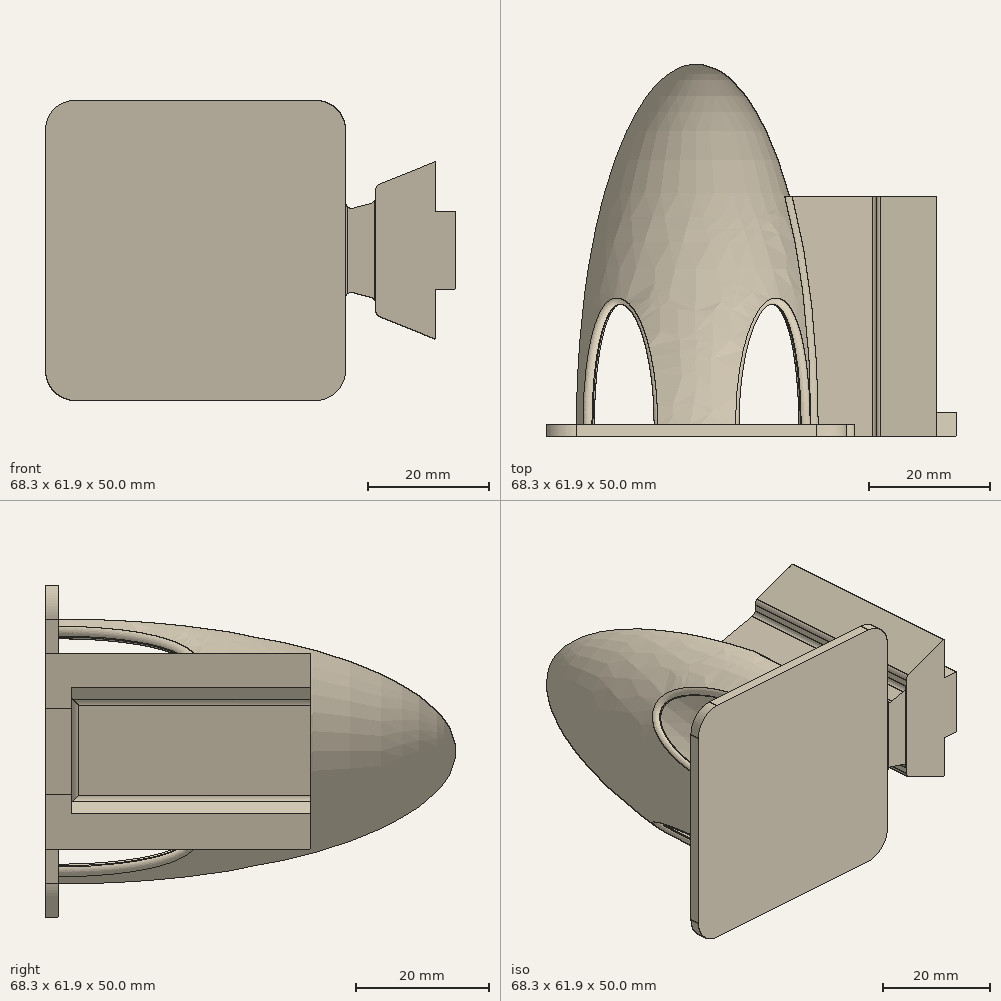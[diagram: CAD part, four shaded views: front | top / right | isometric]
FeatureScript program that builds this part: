
annotation { "Feature Type Name" : "Feature", "Feature Type Description" : "" }
export const myFeature = defineFeature(function(context is Context, id is Id, definition is map)
    precondition{}
    {
        {
            var Q0;
            Q0=qCreatedBy(makeId("Top.planeOp"),FACE);
            var sketch = newSketch(context, id + "F0", { "sketchPlane" : qUnion([Q0])});
            skEllipticalArc(sketch, "E0", {});
            skEllipticalArc(sketch, "E1", {});
            skLineSegment(sketch, "E2", {"start": v(-20, 0) * mm, "end": v(-18, 0) * mm});
            skPoint(sketch, "E2.endSnap0", {"position": v(20, 0) * mm});
            skPoint(sketch, "E3.middle", {"position": v(0, 60) * mm});
            skPoint(sketch, "E4.orphan", {"position": v(0.5, 57.5) * mm});
            skPoint(sketch, "E5.orphan", {"position": v(-0.5, 57.5) * mm});
            skPoint(sketch, "E3.top.end.orphan", {"position": v(-0.5, 62.5) * mm});
            skPoint(sketch, "E3.top.start.orphan", {"position": v(0.5, 62.5) * mm});
            skEllipticalArc(sketch, "E6.trimOffspring", {});
            skPoint(sketch, "E7.orphan", {"position": v(28.84, 0) * mm});
            skPoint(sketch, "E8.orphan", {"position": v(-25.2, 0) * mm});
            skLineSegment(sketch, "E9", {"start": v(0, -14.74) * mm, "end": v(0, 70.43) * mm, "construction": true});
            skLineSegment(sketch, "E10.left", {"start": v(1, 57.91) * mm, "end": v(1, 59.92) * mm});
            skLineSegment(sketch, "E10.right", {"start": v(-1, 57.91) * mm, "end": v(-1, 59.92) * mm});
            skPoint(sketch, "E11.orphan", {"position": v(-1, 58.5) * mm});
            skPoint(sketch, "E12.orphan", {"position": v(1, 58.5) * mm});
            skEllipticalArc(sketch, "E13.trimOffspring", {});
            skPoint(sketch, "E14.orphan", {"position": v(1, 61.5) * mm});
            skPoint(sketch, "E10.top.end.orphan", {"position": v(-1, 61.5) * mm});
            skLineSegment(sketch, "E15.trimOffspring", {"start": v(18, 0) * mm, "end": v(20, 0) * mm});
            const initialGuessF0  = {"E0": [0, 0, 0, 1, 0.06, 0.02, 0.05002085680577006, 1.5707963267948966], "E1": [0, 0, 0, -1, 0.058, 0.018, 1.5707963267948966, 3.086008480308876], "E6.trimOffspring": [0, 0, 0, 1, 0.06, 0.02, 4.71238898038469, 6.233164450373817], "E13.trimOffspring": [0, 0, 0, -1, 0.058, 0.018, 3.197176826870708, 4.71238898038469]};
            skSetInitialGuess(sketch, initialGuessF0);
            skSolve(sketch);
        }
        {
            var Q0;
            {var subQ0=sQuery(id+"F0.wireOp",EDGE,"E0");Q0=makeQuery(id+"F0.imprint","IMPRINT",FACE,{"disambiguationData":[TD([[makeQuery(id+"F0.imprint","IMPRINT",EDGE,{"derivedFrom":subQ0}),1.0]])]});}
            var Q1;
            {var subQ3=sQuery(id+"F0.wireOp",EDGE,"E3.left");Q1=makeQuery(id+"F0.imprint","IMPRINT",FACE,{"disambiguationData":[TD([[makeQuery(id+"F0.imprint","IMPRINT",EDGE,{"derivedFrom":subQ3}),-1.0]])]});}
            var Q2;
            Q2 = qSketchRegion(id + "F3", true);
            var Q3;
            Q3=sQuery(id+"F0.wireOp",EDGE,"E9");
            revolve(context, id + "F1", {"entities" : qUnion([Q0, Q1, Q2]), "axis" : qUnion([Q3]), "revolveType" : RevolveType.FULL, "surfaceOperationType" : NewSurfaceOperationType.NEW});
        }
        {
            var Q0;
            Q0=qCreatedBy(makeId("Top.planeOp"),FACE);
            var Q1;
            Q1=qCreatedBy(makeId("Right.planeOp"),FACE);
            cPlane(context, id + "F2", {"entities" : qUnion([Q0, Q1]), "cplaneType" : CPlaneType.MID_PLANE, "offset" : 25 * mm, "width" : 150 * mm, "height" : 150 * mm});
        }
        {
            var Q0;
            Q0=qCreatedBy(id+"F2.planeOp",FACE);
            var sketch = newSketch(context, id + "F3", { "sketchPlane" : qUnion([Q0])});
            skEllipse(sketch, "E16", {"center": v(0, 0) * mm, "majorRadius": 20 * mm, "minorRadius": 7.5 * mm, "majorAxis": v(-1, 0)});
            skSolve(sketch);
        }
        {
            var Q0;
            Q0 = qSketchRegion(id + "F3", true);
            extrude(context, id + "F4", {"entities" : qUnion([Q0]), "operationType" : NewBodyOperationType.REMOVE, "oppositeDirection" : true, "depth" : 101 * mm, "symmetric" : true});
        }
        {
            var Q0;
            Q0=qCreatedBy(makeId("Right.planeOp"),FACE);
            var Q1;
            Q1=qCreatedBy(makeId("Top.planeOp"),FACE);
            cPlane(context, id + "F5", {"entities" : qUnion([Q0, Q1]), "cplaneType" : CPlaneType.MID_PLANE, "offset" : 25 * mm, "flipAlignment" : true, "width" : 150 * mm, "height" : 150 * mm});
        }
        {
            var Q0;
            Q0=qCreatedBy(id+"F5.planeOp",FACE);
            var sketch = newSketch(context, id + "F6", { "sketchPlane" : qUnion([Q0])});
            skEllipse(sketch, "E17", {"center": v(0, 0) * mm, "majorRadius": 20 * mm, "minorRadius": 7.5 * mm, "majorAxis": v(-1, 0)});
            skSolve(sketch);
        }
        {
            var Q0;
            Q0=makeQuery(id+"F6.imprint","IMPRINT",FACE,{"disambiguationData":[TD([[makeQuery(id+"F6.imprint","IMPRINT",EDGE,{"derivedFrom":sQuery(id+"F6.wireOp",EDGE,"E17")}),1.0]])]});
            extrude(context, id + "F7", {"entities" : qUnion([Q0]), "operationType" : NewBodyOperationType.REMOVE, "oppositeDirection" : true, "depth" : 150 * mm, "symmetric" : true});
        }
        {
            var Q0;
            Q0=qCreatedBy(makeId("Front.planeOp"),FACE);
            cPlane(context, id + "F8", {"entities" : qUnion([Q0]), "cplaneType" : CPlaneType.OFFSET, "offset" : 0 * mm, "width" : 150 * mm, "height" : 150 * mm});
        }
        {
            var Q0;
            Q0=qCreatedBy(id+"F8.planeOp",FACE);
            var sketch = newSketch(context, id + "F9", { "sketchPlane" : qUnion([Q0])});
            skLineSegment(sketch, "E18.bottom", {"start": v(20, -25) * mm, "end": v(-20, -25) * mm});
            skLineSegment(sketch, "E18.top", {"start": v(20, 25) * mm, "end": v(-20, 25) * mm});
            skLineSegment(sketch, "E18.left", {"start": v(25, -20) * mm, "end": v(25, 20) * mm});
            skLineSegment(sketch, "E18.right", {"start": v(-25, -20) * mm, "end": v(-25, 20) * mm});
            skPoint(sketch, "E18.middle", {"position": v(0, 0) * mm});
            skPoint(sketch, "E19.visualSharp", {"position": v(-25, 25) * mm});
            skArc(sketch, "E19.filletArc", {"start": v(-20, 25) * mm, "mid": v(-23.54, 23.54) * mm, "end": v(-25, 20) * mm});
            skPoint(sketch, "E20.visualSharp", {"position": v(25, 25) * mm});
            skArc(sketch, "E20.filletArc", {"start": v(25, 20) * mm, "mid": v(23.54, 23.54) * mm, "end": v(20, 25) * mm});
            skPoint(sketch, "E21.visualSharp", {"position": v(25, -25) * mm});
            skArc(sketch, "E21.filletArc", {"start": v(20, -25) * mm, "mid": v(23.54, -23.54) * mm, "end": v(25, -20) * mm});
            skPoint(sketch, "E22.visualSharp", {"position": v(-25, -25) * mm});
            skArc(sketch, "E22.filletArc", {"start": v(-25, -20) * mm, "mid": v(-23.54, -23.54) * mm, "end": v(-20, -25) * mm});
            skSolve(sketch);
        }
        {
            var Q0;
            Q0 = qSketchRegion(id + "F9", true);
            extrude(context, id + "F10", {"entities" : qUnion([Q0]), "operationType" : NewBodyOperationType.ADD, "depth" : 2 * mm});
        }
        {
            var Q0;
            Q0=sQuery(id+"F9.wireOp",VERTEX,"E18.middle");
            var Q1;
            Q1=makeQuery(id+"F1.opRevolve","SWEPT_BODY",BODY,{"disambiguationData":[OSD([sQuery(id+"F0.wireOp",EDGE,"E0"),sQuery(id+"F0.wireOp",EDGE,"E2"),sQuery(id+"F0.wireOp",EDGE,"E10.right"),sQuery(id+"F0.wireOp",EDGE,"E13.trimOffspring")])]});
            hole(context, id + "F11", {"style" : HoleStyle.SIMPLE, "endStyle" : HoleEndStyle.BLIND, "oppositeDirection" : true, "holeDiameter" : 2 * mm, "holeDepth" : 1 * mm, "startFromSketch" : true, "locations" : qUnion([Q0]), "scope" : qUnion([Q1])});
        }
        {
            var Q0;
            Q0=makeQuery(id+"F10.opExtrude","CAP_FACE",FACE,{"disambiguationData":[OSD([sQuery(id+"F9.wireOp",EDGE,"E18.bottom"),sQuery(id+"F9.wireOp",EDGE,"E18.top"),sQuery(id+"F9.wireOp",EDGE,"E18.left"),sQuery(id+"F9.wireOp",EDGE,"E18.right"),sQuery(id+"F9.wireOp",EDGE,"E19.filletArc"),sQuery(id+"F9.wireOp",EDGE,"E20.filletArc"),sQuery(id+"F9.wireOp",EDGE,"E21.filletArc"),sQuery(id+"F9.wireOp",EDGE,"E22.filletArc")])],"isStart":false});
            var sketch = newSketch(context, id + "F12", { "sketchPlane" : qUnion([Q0])});
            skLineSegment(sketch, "E23", {"start": v(30, 10.75) * mm, "end": v(30, 3.84) * mm});
            skLineSegment(sketch, "E24", {"start": v(40, 14.8) * mm, "end": v(40, 6.5) * mm});
            skPoint(sketch, "E25.middle", {"position": v(30, 0) * mm});
            skLineSegment(sketch, "E26", {"start": v(30, 10.75) * mm, "end": v(40, 14.8) * mm});
            skLineSegment(sketch, "E27", {"start": v(30, -10.75) * mm, "end": v(40, -14.8) * mm});
            skLineSegment(sketch, "E28.trimOffspring", {"start": v(30, -3.84) * mm, "end": v(30, -10.75) * mm});
            skLineSegment(sketch, "E29.bottom", {"start": v(43.3, -6.5) * mm, "end": v(40, -6.5) * mm});
            skLineSegment(sketch, "E29.top", {"start": v(43.3, 6.5) * mm, "end": v(40, 6.5) * mm});
            skLineSegment(sketch, "E29.left", {"start": v(43.3, -6.5) * mm, "end": v(43.3, 6.5) * mm});
            skLineSegment(sketch, "E30.trimOffspring", {"start": v(40, -6.5) * mm, "end": v(40, -14.8) * mm});
            skLineSegment(sketch, "E31", {"start": v(30, 3.84) * mm, "end": v(30, -3.84) * mm});
            skSolve(sketch);
        }
        {
            var Q0;
            Q0 = qSketchRegion(id + "F12", true);
            extrude(context, id + "F13", {"entities" : qUnion([Q0]), "oppositeDirection" : true, "depth" : 40 * mm});
        }
        {
            var Q0;
            {var subQ0=sQuery(id+"F12.wireOp",EDGE,"E29.top");var subQ1=sQuery(id+"F12.wireOp",EDGE,"E27");var subQ2=sQuery(id+"F12.wireOp",EDGE,"E26");var subQ3=sQuery(id+"F12.wireOp",EDGE,"E29.bottom");var subQ4=sQuery(id+"F12.wireOp",EDGE,"E25.top");var subQ5=sQuery(id+"F12.wireOp",EDGE,"E25.bottom");var subQ6=sQuery(id+"F12.wireOp",EDGE,"E28.trimOffspring");var subQ7=sQuery(id+"F12.wireOp",EDGE,"E23");var subQ8=sQuery(id+"F12.wireOp",EDGE,"E24");var subQ9=sQuery(id+"F12.wireOp",EDGE,"E29.left");var subQ10=sQuery(id+"F12.wireOp",EDGE,"E30.trimOffspring");Q0=makeQuery(id+"F13.boolean.opBoolean","SPLIT",FACE,{"disambiguationData":[TD([makeQuery(id+"F1.opRevolve","SWEPT_FACE",FACE,{"disambiguationData":[OSD([sQuery(id+"F0.wireOp",EDGE,"64f7480b-f7c1-41a7-9161-91fdca635b13.0")])]})])],"derivedFrom":makeQuery(id+"F13.opExtrude","CAP_FACE",FACE,{"disambiguationData":[OSD([subQ7,subQ8,subQ5,subQ4,sQuery(id+"F12.wireOp",EDGE,"E25.left"),subQ2,subQ1,subQ6,subQ3,subQ0,subQ9,subQ10])],"isStart":false})});}
            cPlane(context, id + "F14", {"entities" : qUnion([Q0]), "cplaneType" : CPlaneType.OFFSET, "offset" : 36 * mm, "oppositeDirection" : true, "width" : 150 * mm, "height" : 150 * mm});
        }
        {
            var Q0;
            Q0=qCreatedBy(id+"F14.planeOp",FACE);
            var sketch = newSketch(context, id + "F15", { "sketchPlane" : qUnion([Q0])});
            skPoint(sketch, "E32.middle", {"position": v(-35, 0.14) * mm});
            skLineSegment(sketch, "E33", {"start": v(-35, -7.36) * mm, "end": v(-41.98, -10.18) * mm});
            skLineSegment(sketch, "E34", {"start": v(-35, 7.64) * mm, "end": v(-41.98, 10.47) * mm});
            skLineSegment(sketch, "E35", {"start": v(-35, 7.64) * mm, "end": v(-35, -7.36) * mm});
            skLineSegment(sketch, "E36", {"start": v(-41.98, -10.18) * mm, "end": v(-56.76, -10.18) * mm});
            skLineSegment(sketch, "E37", {"start": v(-56.76, -10.18) * mm, "end": v(-56.76, 10.47) * mm});
            skLineSegment(sketch, "E38", {"start": v(-56.76, 10.47) * mm, "end": v(-41.98, 10.47) * mm});
            skSolve(sketch);
        }
        {
            var Q0;
            Q0 = qSketchRegion(id + "F15", true);
            extrude(context, id + "F16", {"entities" : qUnion([Q0]), "operationType" : NewBodyOperationType.REMOVE, "depth" : 50 * mm});
        }
        {
            var Q0;
            Q0=qCreatedBy(makeId("Top.planeOp"),FACE);
            var sketch = newSketch(context, id + "F17", { "sketchPlane" : qUnion([Q0])});
            skLineSegment(sketch, "E39", {"start": v(19.26, -1.97) * mm, "end": v(32.88, -1.97) * mm});
            skLineSegment(sketch, "E40", {"start": v(32.88, -1.97) * mm, "end": v(32.88, 38) * mm});
            skLineSegment(sketch, "E41", {"start": v(32.88, 38) * mm, "end": v(14.68, 38) * mm});
            skFitSpline(sketch, "E42", {"points": [v(19.26, -1.97) * mm, v(14.68, 38) * mm], "startDerivative": vector(1.24, 41.82) * mm, "endDerivative": vector(-10.35, 36.32) * mm});
            skSolve(sketch);
        }
        {
            var Q0;
            Q0 = qSketchRegion(id + "F17", true);
            var Q1;
            Q1=sQuery(id+"F0.wireOp",EDGE,"E9");
            revolve(context, id + "F18", {"operationType" : NewBodyOperationType.ADD, "entities" : qUnion([Q0]), "axis" : qUnion([Q1]), "revolveType" : RevolveType.SYMMETRIC, "angle" : 30 * degree});
        }
        {
            var Q0;
            Q0=makeQuery(id+"F18.boolean.opBoolean","INTERSECT",EDGE,{"disambiguationData":[OD(1.0)],"derivedFrom":[makeQuery(id+"F1.opRevolve","SWEPT_FACE",FACE,{"disambiguationData":[OSD([sQuery(id+"F0.wireOp",EDGE,"E0")])]}),makeQuery(id+"F18.opRevolve","CAP_FACE",FACE,{"disambiguationData":[OSD([sQuery(id+"F17.wireOp",EDGE,"E39"),sQuery(id+"F17.wireOp",EDGE,"E40"),sQuery(id+"F17.wireOp",EDGE,"E41"),sQuery(id+"F17.wireOp",EDGE,"E42")])],"isStart":true})]});
            var Q1;
            Q1=makeQuery(id+"F18.boolean.opBoolean","INTERSECT",EDGE,{"disambiguationData":[OD(1.0)],"derivedFrom":[makeQuery(id+"F1.opRevolve","SWEPT_FACE",FACE,{"disambiguationData":[OSD([sQuery(id+"F0.wireOp",EDGE,"E0")])]}),makeQuery(id+"F18.opRevolve","CAP_FACE",FACE,{"disambiguationData":[OSD([sQuery(id+"F17.wireOp",EDGE,"E39"),sQuery(id+"F17.wireOp",EDGE,"E40"),sQuery(id+"F17.wireOp",EDGE,"E41"),sQuery(id+"F17.wireOp",EDGE,"E42")])],"isStart":false})]});
            var Q2;
            Q2=makeQuery(id+"F18.boolean.opBoolean","INTERSECT",EDGE,{"derivedFrom":[makeQuery(id+"F13.opExtrude","SWEPT_FACE",FACE,{"disambiguationData":[OSD([sQuery(id+"F12.wireOp",EDGE,"E23"),sQuery(id+"F12.wireOp",EDGE,"E28.trimOffspring"),sQuery(id+"F12.wireOp",EDGE,"E31")])]}),makeQuery(id+"F18.opRevolve","CAP_FACE",FACE,{"disambiguationData":[OSD([sQuery(id+"F17.wireOp",EDGE,"E39"),sQuery(id+"F17.wireOp",EDGE,"E40"),sQuery(id+"F17.wireOp",EDGE,"E41"),sQuery(id+"F17.wireOp",EDGE,"E42")])],"isStart":true})]});
            var Q3;
            Q3=makeQuery(id+"F18.boolean.opBoolean","INTERSECT",EDGE,{"derivedFrom":[makeQuery(id+"F13.opExtrude","SWEPT_FACE",FACE,{"disambiguationData":[OSD([sQuery(id+"F12.wireOp",EDGE,"E23"),sQuery(id+"F12.wireOp",EDGE,"E28.trimOffspring"),sQuery(id+"F12.wireOp",EDGE,"E31")])]}),makeQuery(id+"F18.opRevolve","CAP_FACE",FACE,{"disambiguationData":[OSD([sQuery(id+"F17.wireOp",EDGE,"E39"),sQuery(id+"F17.wireOp",EDGE,"E40"),sQuery(id+"F17.wireOp",EDGE,"E41"),sQuery(id+"F17.wireOp",EDGE,"E42")])],"isStart":false})]});
            var Q4;
            {var subQ0=sQuery(id+"F0.wireOp",EDGE,"E2");var subQ1=sQuery(id+"F0.wireOp",EDGE,"E1");var subQ2=makeQuery(id+"F0.imprint","INTERSECT",VERTEX,{"disambiguationData":[OD(0.0)],"derivedFrom":[subQ1,subQ0]});var subQ3=sQuery(id+"F0.wireOp",EDGE,"E6.trimOffspring");var subQ4=makeQuery(id+"F1.opRevolve","SWEPT_FACE",FACE,{"disambiguationData":[OSD([subQ0]),TDD([makeQuery(id+"F0.imprint","IMPRINT",EDGE,{"disambiguationData":[TD([[subQ2,-1.0]])],"derivedFrom":subQ0})])]});var subQ5=makeQuery(id+"F1.opRevolve","SWEPT_FACE",FACE,{"disambiguationData":[OSD([subQ3])]});var subQ6=makeQuery(id+"F4.opExtrude","SWEPT_FACE",FACE,{"disambiguationData":[OSD([sQuery(id+"F3.wireOp",EDGE,"E16")])]});var subQ8=sQuery(id+"F0.wireOp",EDGE,"E0");var subQ9=makeQuery(id+"F1.opRevolve","SWEPT_FACE",FACE,{"disambiguationData":[OSD([subQ8])]});var subQ10=makeQuery(id+"F0.imprint","INTERSECT",VERTEX,{"disambiguationData":[OD(1.0)],"derivedFrom":[subQ1,subQ0]});var subQ11=makeQuery(id+"F1.opRevolve","SWEPT_FACE",FACE,{"disambiguationData":[OSD([subQ0]),TDD([makeQuery(id+"F0.imprint","IMPRINT",EDGE,{"disambiguationData":[TD([[makeQuery(id+"F0.imprint","INTERSECT",VERTEX,{"derivedFrom":[subQ8,subQ0]}),-1.0]])],"derivedFrom":subQ0})])]});Q4=makeQuery(id+"F10.boolean.opBoolean","MERGE",EDGE,{"derivedFrom":[makeQuery(id+"F7.boolean.opBoolean","SPLIT",EDGE,{"disambiguationData":[TD([makeQuery(id+"F4.boolean.opBoolean","COPY",FACE,{"disambiguationData":[TD([subQ9,makeQuery(id+"F1.opRevolve","SWEPT_FACE",FACE,{"disambiguationData":[OSD([subQ1]),TDD([makeQuery(id+"F0.imprint","IMPRINT",EDGE,{"disambiguationData":[TD([[subQ10,1.0]])],"derivedFrom":subQ1})])]}),subQ11]),OD(0.0)],"derivedFrom":subQ6})])],"derivedFrom":makeQuery(id+"F4.boolean.opBoolean","SPLIT",EDGE,{"disambiguationData":[OD(0.0)],"derivedFrom":makeQuery(id+"F1.opRevolve","SWEPT_EDGE",EDGE,{"disambiguationData":[OSD([subQ8,subQ0])]})})}),makeQuery(id+"F7.boolean.opBoolean","SPLIT",EDGE,{"disambiguationData":[TD([makeQuery(id+"F4.boolean.opBoolean","COPY",FACE,{"disambiguationData":[TD([makeQuery(id+"F1.opRevolve","SWEPT_FACE",FACE,{"disambiguationData":[OSD([subQ1]),TDD([makeQuery(id+"F0.imprint","IMPRINT",EDGE,{"disambiguationData":[TD([[subQ2,-1.0]])],"derivedFrom":subQ1})])]}),subQ4,subQ5]),OD(0.0)],"derivedFrom":subQ6})])],"derivedFrom":makeQuery(id+"F4.boolean.opBoolean","SPLIT",EDGE,{"disambiguationData":[OD(0.0)],"derivedFrom":makeQuery(id+"F1.opRevolve","SWEPT_EDGE",EDGE,{"disambiguationData":[OSD([subQ0,subQ3])]})})})]});}
            var Q5;
            {var subQ0=sQuery(id+"F0.wireOp",EDGE,"E2");var subQ1=sQuery(id+"F0.wireOp",EDGE,"E1");var subQ2=makeQuery(id+"F0.imprint","INTERSECT",VERTEX,{"disambiguationData":[OD(0.0)],"derivedFrom":[subQ1,subQ0]});var subQ3=sQuery(id+"F0.wireOp",EDGE,"E6.trimOffspring");var subQ4=makeQuery(id+"F1.opRevolve","SWEPT_FACE",FACE,{"disambiguationData":[OSD([subQ0]),TDD([makeQuery(id+"F0.imprint","IMPRINT",EDGE,{"disambiguationData":[TD([[subQ2,-1.0]])],"derivedFrom":subQ0})])]});var subQ5=makeQuery(id+"F1.opRevolve","SWEPT_FACE",FACE,{"disambiguationData":[OSD([subQ3])]});var subQ6=makeQuery(id+"F4.opExtrude","SWEPT_FACE",FACE,{"disambiguationData":[OSD([sQuery(id+"F3.wireOp",EDGE,"E16")])]});var subQ8=sQuery(id+"F0.wireOp",EDGE,"E0");var subQ9=makeQuery(id+"F1.opRevolve","SWEPT_FACE",FACE,{"disambiguationData":[OSD([subQ8])]});var subQ10=makeQuery(id+"F0.imprint","INTERSECT",VERTEX,{"disambiguationData":[OD(1.0)],"derivedFrom":[subQ1,subQ0]});var subQ11=makeQuery(id+"F1.opRevolve","SWEPT_FACE",FACE,{"disambiguationData":[OSD([subQ0]),TDD([makeQuery(id+"F0.imprint","IMPRINT",EDGE,{"disambiguationData":[TD([[makeQuery(id+"F0.imprint","INTERSECT",VERTEX,{"derivedFrom":[subQ8,subQ0]}),-1.0]])],"derivedFrom":subQ0})])]});Q5=makeQuery(id+"F10.boolean.opBoolean","MERGE",EDGE,{"derivedFrom":[makeQuery(id+"F7.boolean.opBoolean","SPLIT",EDGE,{"disambiguationData":[TD([makeQuery(id+"F4.boolean.opBoolean","COPY",FACE,{"disambiguationData":[TD([subQ9,makeQuery(id+"F1.opRevolve","SWEPT_FACE",FACE,{"disambiguationData":[OSD([subQ1]),TDD([makeQuery(id+"F0.imprint","IMPRINT",EDGE,{"disambiguationData":[TD([[subQ10,1.0]])],"derivedFrom":subQ1})])]}),subQ11]),OD(0.0)],"derivedFrom":subQ6})])],"derivedFrom":makeQuery(id+"F4.boolean.opBoolean","SPLIT",EDGE,{"disambiguationData":[OD(1.0)],"derivedFrom":makeQuery(id+"F1.opRevolve","SWEPT_EDGE",EDGE,{"disambiguationData":[OSD([subQ8,subQ0])]})})}),makeQuery(id+"F7.boolean.opBoolean","SPLIT",EDGE,{"disambiguationData":[TD([makeQuery(id+"F4.boolean.opBoolean","COPY",FACE,{"disambiguationData":[TD([makeQuery(id+"F1.opRevolve","SWEPT_FACE",FACE,{"disambiguationData":[OSD([subQ1]),TDD([makeQuery(id+"F0.imprint","IMPRINT",EDGE,{"disambiguationData":[TD([[subQ2,-1.0]])],"derivedFrom":subQ1})])]}),subQ4,subQ5]),OD(0.0)],"derivedFrom":subQ6})])],"derivedFrom":makeQuery(id+"F4.boolean.opBoolean","SPLIT",EDGE,{"disambiguationData":[OD(1.0)],"derivedFrom":makeQuery(id+"F1.opRevolve","SWEPT_EDGE",EDGE,{"disambiguationData":[OSD([subQ0,subQ3])]})})})]});}
            var Q6;
            {var subQ0=sQuery(id+"F0.wireOp",EDGE,"E2");var subQ1=sQuery(id+"F0.wireOp",EDGE,"E1");var subQ2=makeQuery(id+"F0.imprint","INTERSECT",VERTEX,{"disambiguationData":[OD(0.0)],"derivedFrom":[subQ1,subQ0]});var subQ3=sQuery(id+"F0.wireOp",EDGE,"E6.trimOffspring");var subQ4=makeQuery(id+"F1.opRevolve","SWEPT_FACE",FACE,{"disambiguationData":[OSD([subQ0]),TDD([makeQuery(id+"F0.imprint","IMPRINT",EDGE,{"disambiguationData":[TD([[subQ2,-1.0]])],"derivedFrom":subQ0})])]});var subQ5=makeQuery(id+"F1.opRevolve","SWEPT_FACE",FACE,{"disambiguationData":[OSD([subQ3])]});var subQ6=makeQuery(id+"F4.opExtrude","SWEPT_FACE",FACE,{"disambiguationData":[OSD([sQuery(id+"F3.wireOp",EDGE,"E16")])]});var subQ8=sQuery(id+"F0.wireOp",EDGE,"E0");var subQ9=makeQuery(id+"F1.opRevolve","SWEPT_FACE",FACE,{"disambiguationData":[OSD([subQ8])]});var subQ10=makeQuery(id+"F0.imprint","INTERSECT",VERTEX,{"disambiguationData":[OD(1.0)],"derivedFrom":[subQ1,subQ0]});var subQ11=makeQuery(id+"F1.opRevolve","SWEPT_FACE",FACE,{"disambiguationData":[OSD([subQ0]),TDD([makeQuery(id+"F0.imprint","IMPRINT",EDGE,{"disambiguationData":[TD([[makeQuery(id+"F0.imprint","INTERSECT",VERTEX,{"derivedFrom":[subQ8,subQ0]}),-1.0]])],"derivedFrom":subQ0})])]});Q6=makeQuery(id+"F10.boolean.opBoolean","MERGE",EDGE,{"derivedFrom":[makeQuery(id+"F7.boolean.opBoolean","SPLIT",EDGE,{"disambiguationData":[TD([makeQuery(id+"F4.boolean.opBoolean","COPY",FACE,{"disambiguationData":[TD([subQ9,makeQuery(id+"F1.opRevolve","SWEPT_FACE",FACE,{"disambiguationData":[OSD([subQ1]),TDD([makeQuery(id+"F0.imprint","IMPRINT",EDGE,{"disambiguationData":[TD([[subQ10,1.0]])],"derivedFrom":subQ1})])]}),subQ11]),OD(1.0)],"derivedFrom":subQ6})])],"derivedFrom":makeQuery(id+"F4.boolean.opBoolean","SPLIT",EDGE,{"disambiguationData":[OD(0.0)],"derivedFrom":makeQuery(id+"F1.opRevolve","SWEPT_EDGE",EDGE,{"disambiguationData":[OSD([subQ8,subQ0])]})})}),makeQuery(id+"F7.boolean.opBoolean","SPLIT",EDGE,{"disambiguationData":[TD([makeQuery(id+"F4.boolean.opBoolean","COPY",FACE,{"disambiguationData":[TD([makeQuery(id+"F1.opRevolve","SWEPT_FACE",FACE,{"disambiguationData":[OSD([subQ1]),TDD([makeQuery(id+"F0.imprint","IMPRINT",EDGE,{"disambiguationData":[TD([[subQ2,-1.0]])],"derivedFrom":subQ1})])]}),subQ4,subQ5]),OD(1.0)],"derivedFrom":subQ6})])],"derivedFrom":makeQuery(id+"F4.boolean.opBoolean","SPLIT",EDGE,{"disambiguationData":[OD(0.0)],"derivedFrom":makeQuery(id+"F1.opRevolve","SWEPT_EDGE",EDGE,{"disambiguationData":[OSD([subQ0,subQ3])]})})})]});}
            var Q7;
            Q7=makeQuery(id+"F13.opExtrude","SWEPT_EDGE",EDGE,{"disambiguationData":[OSD([sQuery(id+"F12.wireOp",EDGE,"E27"),sQuery(id+"F12.wireOp",EDGE,"E28.trimOffspring")])]});
            var Q8;
            Q8=makeQuery(id+"F13.opExtrude","SWEPT_EDGE",EDGE,{"disambiguationData":[OSD([sQuery(id+"F12.wireOp",EDGE,"E23"),sQuery(id+"F12.wireOp",EDGE,"E26")])]});
            var Q9;
            Q9=makeQuery(id+"F16.boolean.opBoolean","COPY",EDGE,{"derivedFrom":makeQuery(id+"F16.opExtrude","SWEPT_EDGE",EDGE,{"disambiguationData":[OSD([sQuery(id+"F15.wireOp",EDGE,"E33"),sQuery(id+"F15.wireOp",EDGE,"E35")])]})});
            var Q10;
            Q10=makeQuery(id+"F16.boolean.opBoolean","COPY",EDGE,{"derivedFrom":makeQuery(id+"F16.opExtrude","SWEPT_EDGE",EDGE,{"disambiguationData":[OSD([sQuery(id+"F15.wireOp",EDGE,"E34"),sQuery(id+"F15.wireOp",EDGE,"E35")])]})});
            var Q11;
            Q11=makeQuery(id+"F18.boolean.opBoolean","INTERSECT",EDGE,{"derivedFrom":[makeQuery(id+"F10.opExtrude","SWEPT_FACE",FACE,{"disambiguationData":[OSD([sQuery(id+"F9.wireOp",EDGE,"E18.left")])]}),makeQuery(id+"F18.opRevolve","CAP_FACE",FACE,{"disambiguationData":[OSD([sQuery(id+"F17.wireOp",EDGE,"E39"),sQuery(id+"F17.wireOp",EDGE,"E40"),sQuery(id+"F17.wireOp",EDGE,"E41"),sQuery(id+"F17.wireOp",EDGE,"E42")])],"isStart":true})]});
            var Q12;
            Q12=makeQuery(id+"F18.boolean.opBoolean","INTERSECT",EDGE,{"derivedFrom":[makeQuery(id+"F10.opExtrude","SWEPT_FACE",FACE,{"disambiguationData":[OSD([sQuery(id+"F9.wireOp",EDGE,"E18.left")])]}),makeQuery(id+"F18.opRevolve","SWEPT_FACE",FACE,{"disambiguationData":[OSD([sQuery(id+"F17.wireOp",EDGE,"E39")])]})]});
            var Q13;
            Q13=makeQuery(id+"F18.boolean.opBoolean","INTERSECT",EDGE,{"derivedFrom":[makeQuery(id+"F13.opExtrude","SWEPT_FACE",FACE,{"disambiguationData":[OSD([sQuery(id+"F12.wireOp",EDGE,"E23"),sQuery(id+"F12.wireOp",EDGE,"E28.trimOffspring"),sQuery(id+"F12.wireOp",EDGE,"E31")])]}),makeQuery(id+"F18.opRevolve","SWEPT_FACE",FACE,{"disambiguationData":[OSD([sQuery(id+"F17.wireOp",EDGE,"E39")])]})]});
            var Q14;
            Q14=makeQuery(id+"F18.boolean.opBoolean","INTERSECT",EDGE,{"derivedFrom":[makeQuery(id+"F10.opExtrude","SWEPT_FACE",FACE,{"disambiguationData":[OSD([sQuery(id+"F9.wireOp",EDGE,"E18.left")])]}),makeQuery(id+"F18.opRevolve","CAP_FACE",FACE,{"disambiguationData":[OSD([sQuery(id+"F17.wireOp",EDGE,"E39"),sQuery(id+"F17.wireOp",EDGE,"E40"),sQuery(id+"F17.wireOp",EDGE,"E41"),sQuery(id+"F17.wireOp",EDGE,"E42")])],"isStart":false})]});
            var Q15;
            Q15=makeQuery(id+"F16.boolean.opBoolean","COPY",EDGE,{"derivedFrom":makeQuery(id+"F16.opExtrude","CAP_EDGE",EDGE,{"disambiguationData":[OSD([sQuery(id+"F15.wireOp",EDGE,"E35")])],"isStart":true})});
            fillet(context, id + "F19", {"entities" : qUnion([Q0, Q1, Q2, Q3, Q4, Q5, Q6, Q7, Q8, Q9, Q10, Q11, Q12, Q13, Q14, Q15]), "radius" : 1 * mm, "allowEdgeOverflow" : false});
        }
        {
            var Q0;
            Q0=makeQuery(id+"F7.boolean.opBoolean","INTERSECT",EDGE,{"disambiguationData":[OD(1.0)],"derivedFrom":[makeQuery(id+"F1.opRevolve","SWEPT_FACE",FACE,{"disambiguationData":[OSD([sQuery(id+"F0.wireOp",EDGE,"E0")])]}),makeQuery(id+"F7.opExtrude","SWEPT_FACE",FACE,{"disambiguationData":[OSD([sQuery(id+"F6.wireOp",EDGE,"E17")])]})]});
            var Q1;
            Q1=makeQuery(id+"F7.boolean.opBoolean","INTERSECT",EDGE,{"disambiguationData":[OD(1.0)],"derivedFrom":[makeQuery(id+"F1.opRevolve","SWEPT_FACE",FACE,{"disambiguationData":[OSD([sQuery(id+"F0.wireOp",EDGE,"E13.trimOffspring")])]}),makeQuery(id+"F7.opExtrude","SWEPT_FACE",FACE,{"disambiguationData":[OSD([sQuery(id+"F6.wireOp",EDGE,"E17")])]})]});
            var Q2;
            Q2=makeQuery(id+"F4.boolean.opBoolean","INTERSECT",EDGE,{"disambiguationData":[OD(0.0)],"derivedFrom":[makeQuery(id+"F1.opRevolve","SWEPT_FACE",FACE,{"disambiguationData":[OSD([sQuery(id+"F0.wireOp",EDGE,"E0")])]}),makeQuery(id+"F4.opExtrude","SWEPT_FACE",FACE,{"disambiguationData":[OSD([sQuery(id+"F3.wireOp",EDGE,"E16")])]})]});
            var Q3;
            Q3=makeQuery(id+"F4.boolean.opBoolean","INTERSECT",EDGE,{"disambiguationData":[OD(0.0)],"derivedFrom":[makeQuery(id+"F1.opRevolve","SWEPT_FACE",FACE,{"disambiguationData":[OSD([sQuery(id+"F0.wireOp",EDGE,"E13.trimOffspring")])]}),makeQuery(id+"F4.opExtrude","SWEPT_FACE",FACE,{"disambiguationData":[OSD([sQuery(id+"F3.wireOp",EDGE,"E16")])]})]});
            var Q4;
            Q4=makeQuery(id+"F4.boolean.opBoolean","INTERSECT",EDGE,{"disambiguationData":[OD(1.0)],"derivedFrom":[makeQuery(id+"F1.opRevolve","SWEPT_FACE",FACE,{"disambiguationData":[OSD([sQuery(id+"F0.wireOp",EDGE,"E0")])]}),makeQuery(id+"F4.opExtrude","SWEPT_FACE",FACE,{"disambiguationData":[OSD([sQuery(id+"F3.wireOp",EDGE,"E16")])]})]});
            var Q5;
            Q5=makeQuery(id+"F4.boolean.opBoolean","INTERSECT",EDGE,{"disambiguationData":[OD(1.0)],"derivedFrom":[makeQuery(id+"F1.opRevolve","SWEPT_FACE",FACE,{"disambiguationData":[OSD([sQuery(id+"F0.wireOp",EDGE,"E13.trimOffspring")])]}),makeQuery(id+"F4.opExtrude","SWEPT_FACE",FACE,{"disambiguationData":[OSD([sQuery(id+"F3.wireOp",EDGE,"E16")])]})]});
            var Q6;
            Q6=makeQuery(id+"F7.boolean.opBoolean","INTERSECT",EDGE,{"disambiguationData":[OD(0.0)],"derivedFrom":[makeQuery(id+"F1.opRevolve","SWEPT_FACE",FACE,{"disambiguationData":[OSD([sQuery(id+"F0.wireOp",EDGE,"E0")])]}),makeQuery(id+"F7.opExtrude","SWEPT_FACE",FACE,{"disambiguationData":[OSD([sQuery(id+"F6.wireOp",EDGE,"E17")])]})]});
            var Q7;
            Q7=makeQuery(id+"F7.boolean.opBoolean","INTERSECT",EDGE,{"disambiguationData":[OD(0.0)],"derivedFrom":[makeQuery(id+"F1.opRevolve","SWEPT_FACE",FACE,{"disambiguationData":[OSD([sQuery(id+"F0.wireOp",EDGE,"E13.trimOffspring")])]}),makeQuery(id+"F7.opExtrude","SWEPT_FACE",FACE,{"disambiguationData":[OSD([sQuery(id+"F6.wireOp",EDGE,"E17")])]})]});
            fillet(context, id + "F20", {"entities" : qUnion([Q0, Q1, Q2, Q3, Q4, Q5, Q6, Q7]), "radius" : 0.9 * mm, "tangentPropagation" : true, "allowEdgeOverflow" : false});
        }
    });
